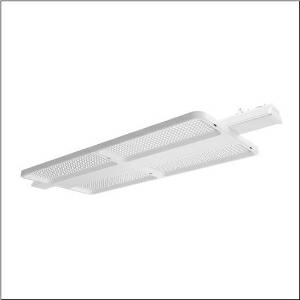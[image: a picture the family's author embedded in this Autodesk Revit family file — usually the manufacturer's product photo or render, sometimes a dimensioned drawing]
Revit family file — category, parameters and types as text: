
# Revit family: highbay_11_fur_licross_r__tragschiene_maxi_51hn12db4rla_582d
name_source: partatom
category: Lighting Fixtures
units: mm (PartAtom-declared; Revit-internal decimal feet)

## family parameters
Cut with Voids When Loaded = No
Host = Face
Light Source = No
Part Type = Normal
Room Calculation Point = No
Round Connector Dimension = Use Diameter
Shared = No

## types (1)
- --- (1 x LED, 42500 lm, 213.7 W, 4000K)
    Apparent Load = 214 VA
    CIE Flux Codes = 87 98 100 100 100
    Color Rendering = 80
    Color Temperature = 4000K
    Default Elevation = 1800 mm
    Description = high bay luminaire Highbay 11 for Licross® trunking rail maxi; direct symmetric wide distribution, light control with lens of PMMA; UGR ≤ 22 (X = 4H | Y = 8H | S = 0.25H | reflection values 70/50/20); luminous flux: 42.500lm; light colour: 840, colour temperature: 4000K, MacAdam ≤ 2 SDCM (initial), colour rendering: CRI > 80; luminous efficacy: 198,9lm/W; rated service life: 100.000h (L95/B50) at AT= 25°C; control: DALI 2; luminaire connection: plug, 5-pole, with phase selectionmains connection: 230..240V, AC 50/60Hz; connected load: 213,7W; protection rating (complete): IP64; insulation class (complete): insulation class I (protective earthing); protection symbol: D; impact resistance: IK07; certification: CE, ENEC, VDE, UKCA; internal wiring halogen-free; luminaire LABS conformity tested according to VDMA 24364:2018-05; corresponds to IFS (International Featured Standards) requirements for safety and quality in the food industry; housing frame of high-performance plastic PA6, matt traffic white (RAL 9016); cover of PMMA; fixing on rail side of steel, galvanised, white; blank cover of PC/ABS, traffic white (RAL 9016); dimension (LxWxH): 1.250 x 442 x 71mm; permissible operating ambient temperature: -40..+50°C (reducing of maximum allowable ambient temperature of 5°C with ceiling mounting); packaging unit: 1 piece
    Height = 72 mm  [stored 0.23622 ft]
    Lamp = 1 x LED
    Lamp Light Flux = 42500 lm
    Lamp Power = 213.7 W
    Lamp count = 1
    Length = 946 mm
    Luminous efficacy = 199 lm/W
    Manufacturer = Siteco
    ModVariant = No
    Model = 51HN12DB4RLA
    Mounting Place = Ceiling
    Mounting Type = Pendant
    Number of Poles = 1
    OnlyDefault = Yes
    Power Factor = 1
    Product Name = Highbay 11 für Licross® Tragschiene maxi
    Product group = high bay luminaire
    ProductGroupID = 901
    Protection Class = Protection class I
    Protection Degree = IP 64
    RLX_Detail_Level = 1
    RLX_Emergency_Light_Flux = 0 lm
    RLX_Emergency_Type = 0
    RLX_Emergency_Type_DB = No
    RlxData = <blob elided: 24277 chars, md5=3b094b77>
    Socket = socket
    Standby Power = 0 W
    System Light Flux = 42501 lm
    System Power = 214 W
    Type Comments = factory setting: luminous flux: 100 % | dim-lin: 254 | 983 mA
    Type Image = l_1361711.jpg
    URL = http://relux.com
    VarID = @adj_014667
    Voltage = 0 V
    Weight = 0.00 kg
    Width = 442 mm

note: [stored X ft] marks values corroborated as IEEE doubles in the binary element streams (Revit-internal decimal feet)

## geometry (parser evidence)
native form markers: Blend x4, Sweep x10
no freeform markers — native parametric forms only
